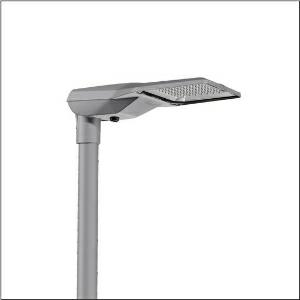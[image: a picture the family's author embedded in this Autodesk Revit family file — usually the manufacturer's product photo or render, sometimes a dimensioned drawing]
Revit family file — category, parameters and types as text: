
# Revit family: streetlight_sl_21_midi___p0_8ab_5xe3r33r08lb_93be
name_source: partatom
category: Lighting Fixtures
units: mm (PartAtom-declared; Revit-internal decimal feet)

## family parameters
Cut with Voids When Loaded = No
Host = Face
Light Source = No
Part Type = Normal
Room Calculation Point = No
Round Connector Dimension = Use Diameter
Shared = No

## types (1)
- --- (1 x LED, 12450 lm, 99.6 W, 3000K)
    Apparent Load = 100 VA
    CIE Flux Codes = 36 71 98 100 100
    Color Rendering = 70
    Color Temperature = 3000K
    Default Elevation = 1800 mm
    Description = Streetlight SL 21 midi, mast luminaire, primary light control with lens, of PMMA, primary optical cover: cover, of toughened safety glass, transparent, light distribution: P0.8aB, light emission: direct distribution, primary light characteristic: asymmetric, installation type: post-top, side-entry, LED, High Power LED, rated luminous flux: 12.450lm, luminous efficacy: 125lm/W, light colour: 730, colour temperature: 3000K, control gear: D4i, control: pre-setting: logarithmic dimming characteristic, flexible luminous flux parameterisation, time-dependent luminous flux control, constant luminous flux control, overheat protection, mains connection: 230..240V, AC, 50/60Hz, start of lifetime: 100W, end of service life: 102W, reduction: 46W, luminaire housing, of diecast aluminium, powder-coated, SITECO metallic grey (DB 702S), corrosivity category C5 high according to DIN EN ISO 12944, multi-level sealing system, sealing non-destructively replaceable, inclination adjustable: 0°, 5°, 10°, 15°, please order mast flange separately, length: 644mm, width: 335mm, height: 110mm, mast flange for spigot size: 42mm (side-entry): 5XC10008XM4, 60/48mm (side-entry/post-top): 5XC10108XM2, 76/60mm (side-entry/post-top): 5XC10108XM1, mounting height: 4..8m, Smart Interface below, protection rating (complete): IP66, insulation class (complete): insulation class II (safety insulation), certification: CE, ENEC, ENEC+, VDE, impact resistance: IK10, permissible operating ambient temperature for outdoor applications: -40..+50°C, standard-compliant lighting for roads and squares, packaging unit: 1 piece

Light Distribution: P0.8aB
    Height = 111 mm
    Lamp = 1 x LED
    Lamp Light Flux = 12450 lm
    Lamp Power = 99.6 W
    Lamp count = 1
    Length = 644 mm
    Luminous efficacy = 125 lm/W
    Manufacturer = Siteco
    ModVariant = No
    Model = 5XE3R33R08LB
    Number of Poles = 1
    OnlyDefault = Yes
    Power Factor = 1
    Product Name = Streetlight SL 21 midi | P0.8aB
    Product group = mast luminaire | pylon top
    ProductGroupID = 6100
    Protection Class = Protection class II
    Protection Degree = IP 66
    RLX_Detail_Level = 1
    RLX_Emergency_Light_Flux = 0 lm
    RLX_Emergency_Type = 0
    RLX_Emergency_Type_DB = No
    RlxData = <blob elided: 26565 chars, md5=ebde02c1>
    Socket = socket
    Standby Power = 0 W
    System Light Flux = 12450 lm
    System Power = 100 W
    Type Comments = factory setting: luminous flux: 100 % | dim-lin: 254 | 1020 mA
    Type Image = l_1004300.jpg
    URL = http://relux.com
    VarID = @adj_033343
    Voltage = 0 V
    Weight = 0.00 kg
    Width = 336 mm

## geometry (parser evidence)
native form markers: Blend x4, Sweep x12
no freeform markers — native parametric forms only
